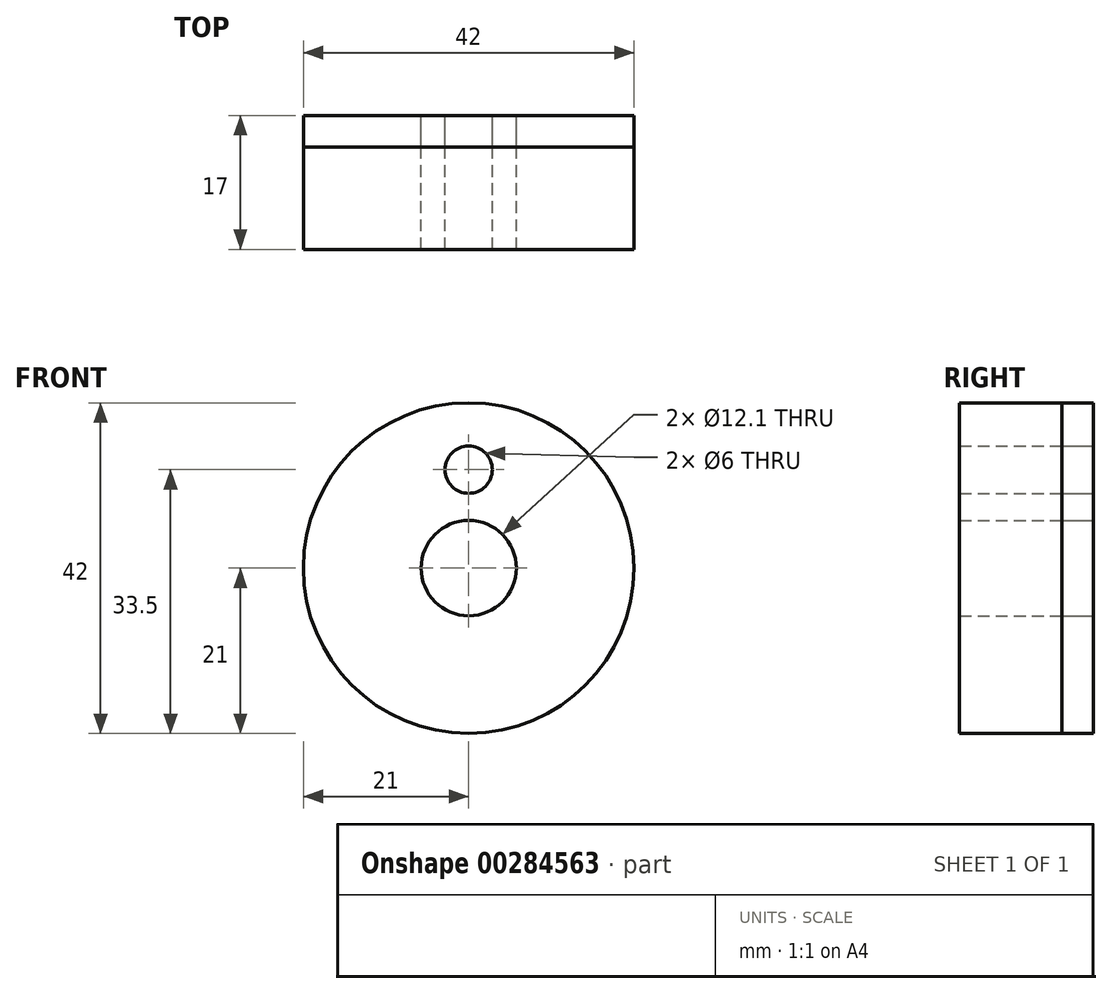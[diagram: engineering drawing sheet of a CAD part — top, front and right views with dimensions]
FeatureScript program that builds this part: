
annotation { "Feature Type Name" : "Feature", "Feature Type Description" : "" }
export const myFeature = defineFeature(function(context is Context, id is Id, definition is map)
    precondition{}
    {
        {
            var Q0;
            Q0=qCreatedBy(makeId("Front.planeOp"),FACE);
            var sketch = newSketch(context, id + "F0", { "sketchPlane" : qUnion([Q0])});
            skCircle(sketch, "E0", {"center": v(0, 0) * mm, "radius": 21 * mm});
            skCircle(sketch, "E1", {"center": v(0, 0) * mm, "radius": 6.05 * mm});
            skPoint(sketch, "E2", {"position": v(0, 12.5) * mm});
            skCircle(sketch, "E3", {"center": v(0, 12.5) * mm, "radius": 3 * mm});
            skSolve(sketch);
        }
        {
            var Q0;
            Q0=makeQuery(id+"F0.imprint","IMPRINT",FACE,{"disambiguationData":[TD([[makeQuery(id+"F0.imprint","IMPRINT",EDGE,{"derivedFrom":sQuery(id+"F0.wireOp",EDGE,"E0")}),1.0]])]});
            extrude(context, id + "F1", {"entities" : qUnion([Q0]), "depth" : 17 * mm});
        }
        {
            var Q0;
            Q0 = qSketchRegion(id + "F0", true);
            extrude(context, id + "F2", {"entities" : qUnion([Q0]), "depth" : 4 * mm});
        }
    });
